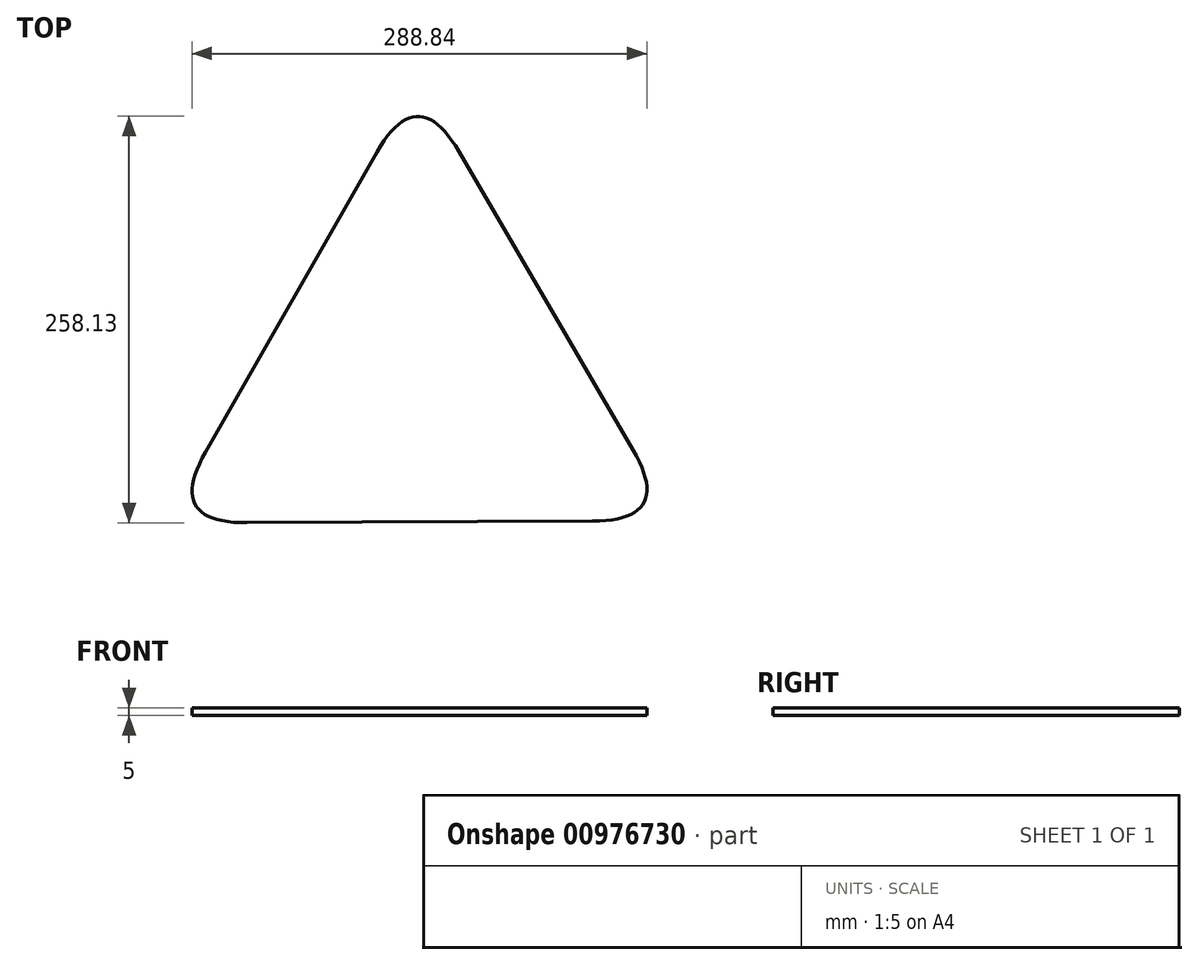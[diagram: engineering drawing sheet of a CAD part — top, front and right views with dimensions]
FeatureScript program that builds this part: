
annotation { "Feature Type Name" : "Feature", "Feature Type Description" : "" }
export const myFeature = defineFeature(function(context is Context, id is Id, definition is map)
    precondition{}
    {
        {
            var Q0;
            Q0=qCreatedBy(makeId("Top.planeOp"),FACE);
            var sketch = newSketch(context, id + "F0", { "sketchPlane" : qUnion([Q0])});
            skCircle(sketch, "E0.cCircle", {"center": v(0.2, 4.48) * mm, "radius": 93.38 * mm, "construction": true});
            skLineSegment(sketch, "E0.0", {"start": v(-161.13, -89.62) * mm, "end": v(-0.64, 191.24) * mm});
            skLineSegment(sketch, "E0.1", {"start": v(-0.64, 191.24) * mm, "end": v(162.35, -88.17) * mm});
            skLineSegment(sketch, "E0.2", {"start": v(162.35, -88.17) * mm, "end": v(-161.13, -89.62) * mm});
            skPoint(sketch, "E0.0.midPoint", {"position": v(-80.88, 50.81) * mm});
            skSolve(sketch);
        }
        {
            var Q0;
            Q0=makeQuery(id+"F0.imprint","IMPRINT",FACE,{"disambiguationData":[TD([[makeQuery(id+"F0.imprint","IMPRINT",EDGE,{"derivedFrom":sQuery(id+"F0.wireOp",EDGE,"E0.0")}),-1.0]])]});
            extrude(context, id + "F1", {"entities" : qUnion([Q0]), "depth" : 5 * mm, "offsetDistance" : 25 * mm});
        }
        {
            var Q0;
            Q0=makeQuery(id+"F1.opExtrude","SWEPT_EDGE",EDGE,{"disambiguationData":[OSD([sQuery(id+"F0.wireOp",EDGE,"E0.0"),sQuery(id+"F0.wireOp",EDGE,"E0.1")])]});
            var Q1;
            Q1=makeQuery(id+"F1.opExtrude","SWEPT_EDGE",EDGE,{"disambiguationData":[OSD([sQuery(id+"F0.wireOp",EDGE,"E0.0"),sQuery(id+"F0.wireOp",EDGE,"E0.2")])]});
            var Q2;
            Q2=makeQuery(id+"F1.opExtrude","SWEPT_EDGE",EDGE,{"disambiguationData":[OSD([sQuery(id+"F0.wireOp",EDGE,"E0.1"),sQuery(id+"F0.wireOp",EDGE,"E0.2")])]});
            fillet(context, id + "F2", {"entities" : qUnion([Q0, Q1, Q2]), "radius" : 30 * mm, "tangentPropagation" : true, "rho" : 0.5, "crossSection" : FilletCrossSection.CONIC, "allowEdgeOverflow" : false});
        }
    });
